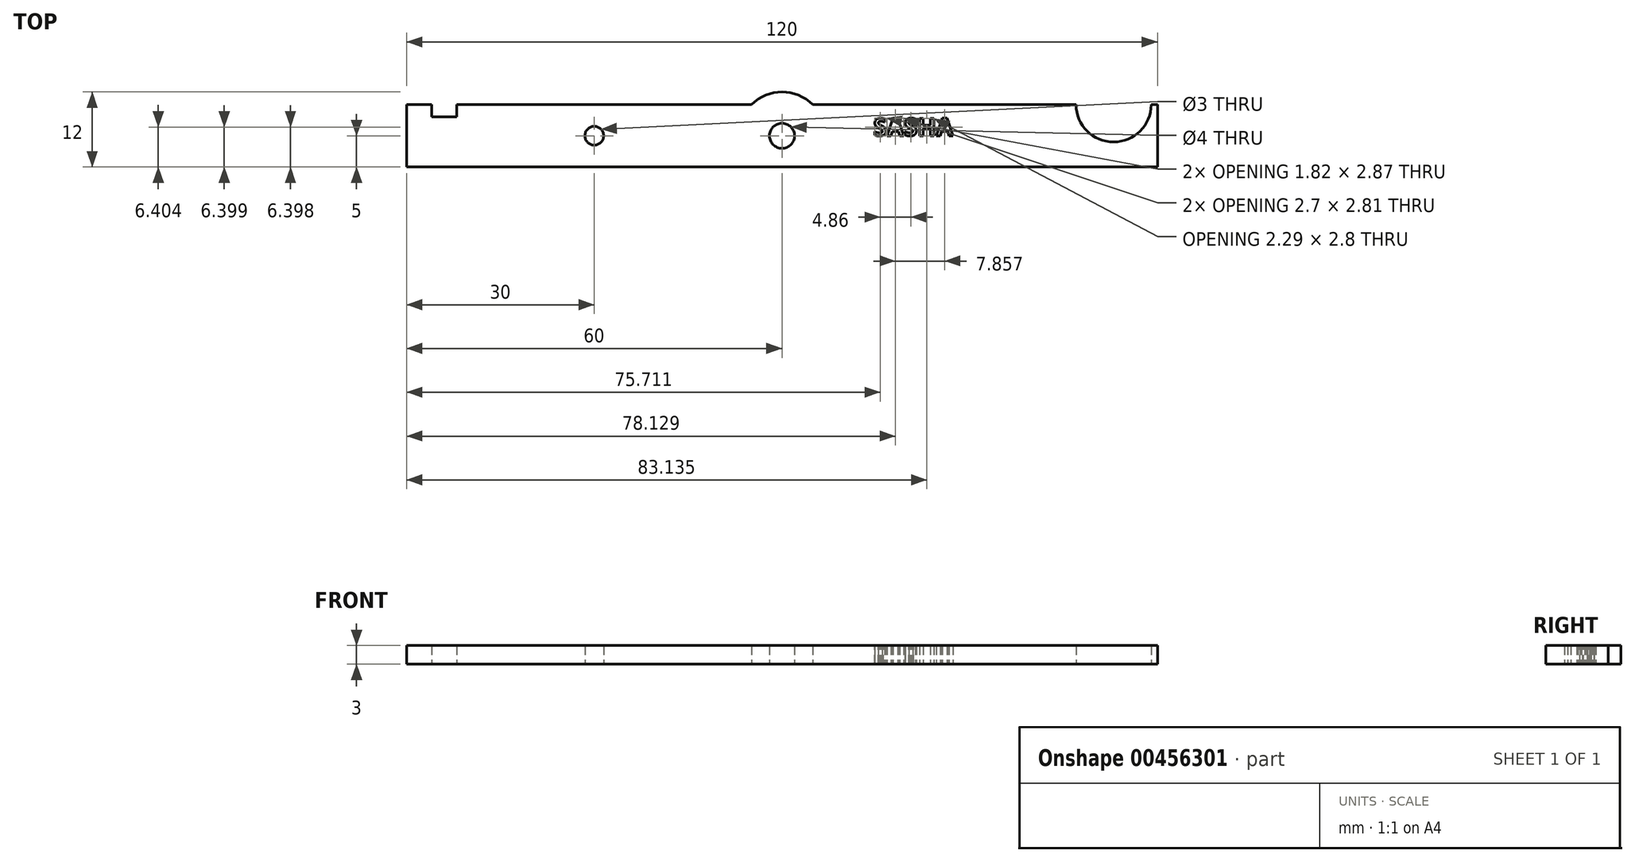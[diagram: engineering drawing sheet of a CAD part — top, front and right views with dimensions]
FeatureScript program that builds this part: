
annotation { "Feature Type Name" : "Feature", "Feature Type Description" : "" }
export const myFeature = defineFeature(function(context is Context, id is Id, definition is map)
    precondition{}
    {
        {
            var Q0;
            Q0=qCreatedBy(makeId("Top.planeOp"),FACE);
            var sketch = newSketch(context, id + "F0", { "sketchPlane" : qUnion([Q0])});
            skLineSegment(sketch, "E0.bottom", {"start": v(-60, 5) * mm, "end": v(60, 5) * mm});
            skLineSegment(sketch, "E0.top", {"start": v(-60, -5) * mm, "end": v(60, -5) * mm});
            skLineSegment(sketch, "E0.left", {"start": v(-60, 5) * mm, "end": v(-60, -5) * mm});
            skLineSegment(sketch, "E0.right", {"start": v(60, 5) * mm, "end": v(60, -5) * mm});
            skPoint(sketch, "E0.middle", {"position": v(0, 0) * mm});
            skLineSegment(sketch, "E1.bottom", {"start": v(-52, 5) * mm, "end": v(-56, 5) * mm});
            skLineSegment(sketch, "E1.top", {"start": v(-52, 3) * mm, "end": v(-56, 3) * mm});
            skLineSegment(sketch, "E1.left", {"start": v(-52, 5) * mm, "end": v(-52, 3) * mm});
            skLineSegment(sketch, "E1.right", {"start": v(-56, 5) * mm, "end": v(-56, 3) * mm});
            skCircle(sketch, "E2", {"center": v(0, 0) * mm, "radius": 2 * mm});
            skCircle(sketch, "E3", {"center": v(-30, 0) * mm, "radius": 1.5 * mm});
            skCircle(sketch, "E4", {"center": v(0, 0) * mm, "radius": 7 * mm});
            skCircle(sketch, "E5", {"center": v(-23.23, 65.28) * mm, "radius": 1.5 * mm});
            skCircle(sketch, "E6", {"center": v(53, 5) * mm, "radius": 6 * mm});
            skText(sketch, "E7", { "text": "SASHA", "fontName": "OpenSans-Bold.ttf"});
            const initialGuessF0  = {"E7": [0.01462, 0, 1, 0, 0.00282]};
            skSetInitialGuess(sketch, initialGuessF0);
            skSolve(sketch);
        }
        {
            var Q0;
            {var subQ0=sQuery(id+"F0.wireOp",EDGE,"E0.left");Q0=makeQuery(id+"F0.imprint","IMPRINT",FACE,{"disambiguationData":[TD([[makeQuery(id+"F0.imprint","IMPRINT",EDGE,{"derivedFrom":subQ0}),1.0]])]});}
            var Q1;
            {var subQ0=sQuery(id+"F0.wireOp",EDGE,"E0.right");Q1=makeQuery(id+"F0.imprint","IMPRINT",FACE,{"disambiguationData":[TD([[makeQuery(id+"F0.imprint","IMPRINT",EDGE,{"derivedFrom":subQ0}),-1.0]])]});}
            var Q2;
            Q2=makeQuery(id+"F0.imprint","IMPRINT",FACE,{"disambiguationData":[TD([[makeQuery(id+"F0.imprint","IMPRINT",EDGE,{"derivedFrom":sQuery(id+"F0.wireOp",EDGE,"E2")}),-1.0]])]});
            var Q3;
            {var subQ0=sQuery(id+"F0.wireOp",EDGE,"E4");var subQ1=sQuery(id+"F0.wireOp",EDGE,"E0.bottom");var subQ2=makeQuery(id+"F0.imprint","INTERSECT",VERTEX,{"disambiguationData":[OD(0.0)],"derivedFrom":[subQ1,subQ0]});Q3=makeQuery(id+"F0.imprint","IMPRINT",FACE,{"disambiguationData":[TD([[makeQuery(id+"F0.imprint","IMPRINT",EDGE,{"disambiguationData":[TD([[subQ2,-1.0]])],"derivedFrom":subQ1}),1.0]])]});}
            var Q4;
            {var subQ0=sQuery(id+"F0.wireOp",EDGE,"E4");var subQ1=sQuery(id+"F0.wireOp",EDGE,"E0.top");var subQ2=makeQuery(id+"F0.imprint","INTERSECT",VERTEX,{"disambiguationData":[OD(0.0)],"derivedFrom":[subQ1,subQ0]});Q4=makeQuery(id+"F0.imprint","IMPRINT",FACE,{"disambiguationData":[TD([[makeQuery(id+"F0.imprint","IMPRINT",EDGE,{"disambiguationData":[TD([[subQ2,-1.0]])],"derivedFrom":subQ1}),-1.0]])]});}
            extrude(context, id + "F1", {"entities" : qUnion([Q0, Q1, Q2, Q3, Q4]), "depth" : 3 * mm});
        }
    });
